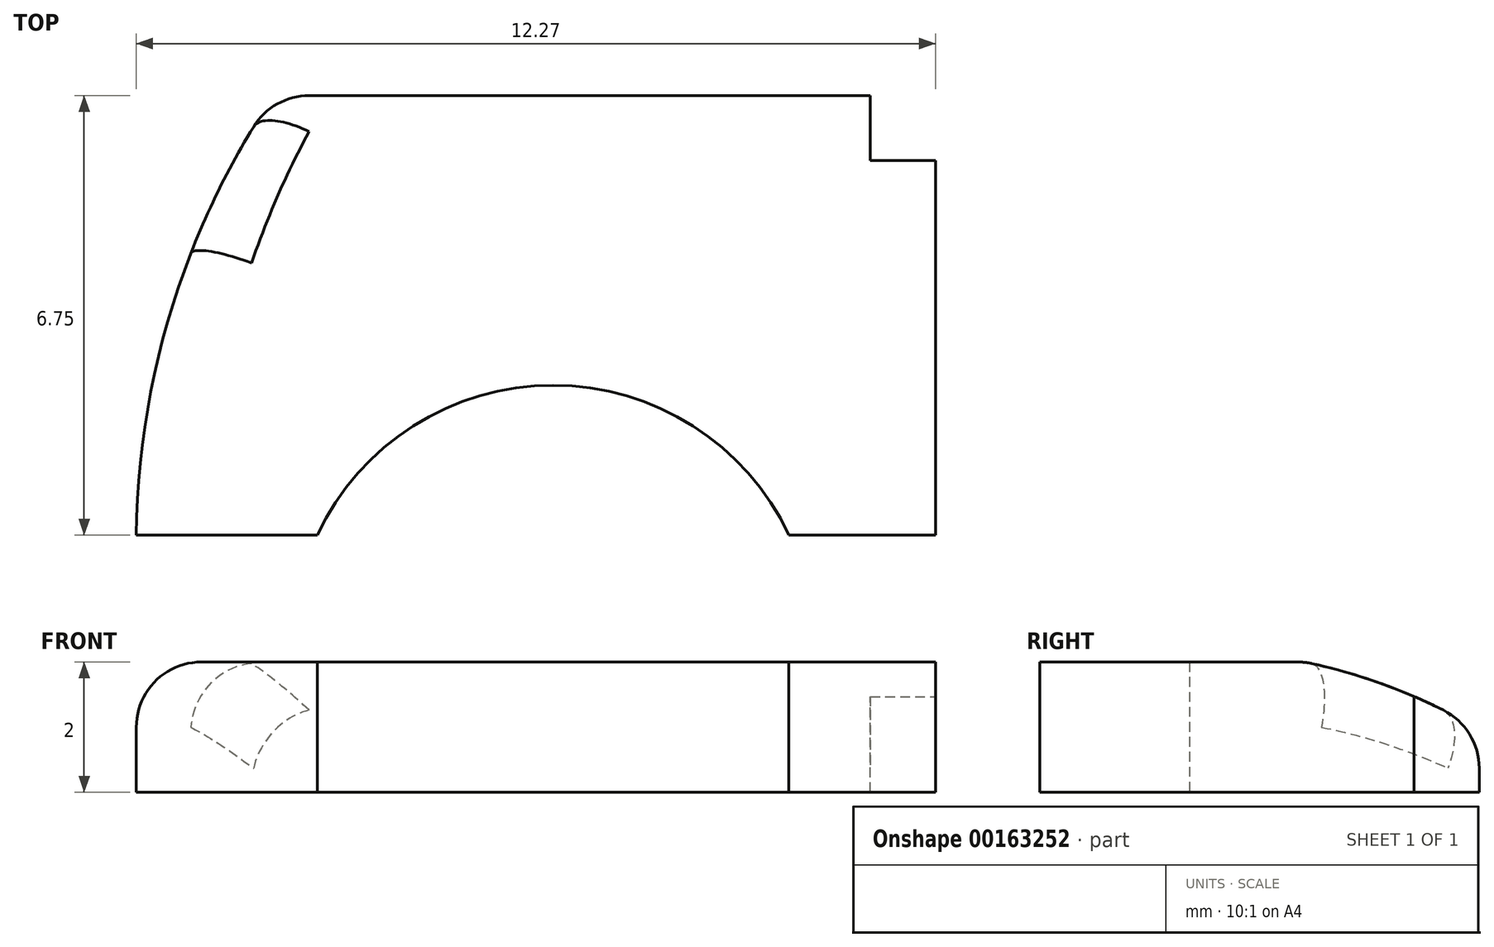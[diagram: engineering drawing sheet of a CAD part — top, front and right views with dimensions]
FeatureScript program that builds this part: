
annotation { "Feature Type Name" : "Feature", "Feature Type Description" : "" }
export const myFeature = defineFeature(function(context is Context, id is Id, definition is map)
    precondition{}
    {
        {
            var Q0;
            Q0=qCreatedBy(makeId("Top.planeOp"),FACE);
            var sketch = newSketch(context, id + "F0", { "sketchPlane" : qUnion([Q0])});
            skArc(sketch, "E0", {"start": v(0, 0) * mm, "mid": v(-3.62, 2.3) * mm, "end": v(-7.24, 0) * mm});
            skLineSegment(sketch, "E1", {"start": v(-7.24, 0) * mm, "end": v(-10.02, 0) * mm});
            skArc(sketch, "E2", {"start": v(-7.91, 6.75) * mm, "mid": v(-9.46, 3.53) * mm, "end": v(-10.02, 0) * mm});
            skLineSegment(sketch, "E3", {"start": v(-7.91, 6.75) * mm, "end": v(2.25, 6.75) * mm});
            skLineSegment(sketch, "E4", {"start": v(2.25, 6.75) * mm, "end": v(2.25, 0) * mm});
            skLineSegment(sketch, "E5", {"start": v(2.25, 0) * mm, "end": v(0, 0) * mm});
            skSolve(sketch);
        }
        {
            var Q0;
            Q0 = qSketchRegion(id + "F0", true);
            extrude(context, id + "F1", {"entities" : qUnion([Q0]), "depth" : 2 * mm});
        }
        {
            var Q0;
            Q0=makeQuery(id+"F1.opExtrude","SWEPT_FACE",FACE,{"disambiguationData":[OSD([sQuery(id+"F0.wireOp",EDGE,"E4")])]});
            var sketch = newSketch(context, id + "F2", { "sketchPlane" : qUnion([Q0])});
            skLineSegment(sketch, "E6", {"start": v(1.3, 1.98) * mm, "end": v(1.3, 1.98) * mm});
            skArc(sketch, "E7", {"start": v(7.25, 0.64) * mm, "mid": v(5.78, 1.46) * mm, "end": v(4.18, 1.98) * mm});
            skPoint(sketch, "E8.visualSharp", {"position": v(8.37, -0.29) * mm});
            skPoint(sketch, "E9.visualSharp", {"position": v(12.01, -0.29) * mm});
            skPoint(sketch, "E10.visualSharp", {"position": v(4.07, 2) * mm});
            skArc(sketch, "E10.filletArc", {"start": v(4.18, 1.98) * mm, "mid": v(4.07, 2) * mm, "end": v(3.96, 2) * mm});
            skLineSegment(sketch, "E11", {"start": v(5.8, 3.91) * mm, "end": v(3.96, 2) * mm});
            skLineSegment(sketch, "E12", {"start": v(5.8, 3.91) * mm, "end": v(8.9, 2.87) * mm});
            skLineSegment(sketch, "E13", {"start": v(8.9, 2.87) * mm, "end": v(7.25, 0.64) * mm});
            skSolve(sketch);
        }
        {
            var Q0;
            Q0 = qSketchRegion(id + "F2", true);
            extrude(context, id + "F3", {"entities" : qUnion([Q0]), "operationType" : NewBodyOperationType.REMOVE, "endBound" : BoundingType.THROUGH_ALL, "oppositeDirection" : true, "depth" : 25 * mm});
        }
        {
            var Q0;
            Q0=makeQuery(id+"F1.opExtrude","SWEPT_EDGE",EDGE,{"disambiguationData":[OSD([sQuery(id+"F0.wireOp",EDGE,"E2"),sQuery(id+"F0.wireOp",EDGE,"E3")])]});
            var Q1;
            Q1=makeQuery(id+"F3.boolean.opBoolean","INTERSECT",EDGE,{"derivedFrom":[makeQuery(id+"F1.opExtrude","SWEPT_FACE",FACE,{"disambiguationData":[OSD([sQuery(id+"F0.wireOp",EDGE,"E2")])]}),makeQuery(id+"F3.opExtrude","SWEPT_FACE",FACE,{"disambiguationData":[OSD([sQuery(id+"F2.wireOp",EDGE,"E7")])]})]});
            fillet(context, id + "F4", {"entities" : qUnion([Q0, Q1]), "radius" : 1 * mm, "tangentPropagation" : true, "allowEdgeOverflow" : false});
        }
        {
            var Q0;
            {var subQ0=sQuery(id+"F0.wireOp",EDGE,"E2");Q0=makeQuery(id+"F4.opFillet","BLEND_EDGE",EDGE,{"blendedFrom":[makeQuery(id+"F1.opExtrude","SWEPT_EDGE",EDGE,{"disambiguationData":[OSD([subQ0,sQuery(id+"F0.wireOp",EDGE,"E3")])]}),makeQuery(id+"F3.boolean.opBoolean","INTERSECT",EDGE,{"derivedFrom":[makeQuery(id+"F1.opExtrude","SWEPT_FACE",FACE,{"disambiguationData":[OSD([subQ0])]}),makeQuery(id+"F3.opExtrude","SWEPT_FACE",FACE,{"disambiguationData":[OSD([sQuery(id+"F2.wireOp",EDGE,"E7")])]})]})],"blendedInto":[]});}
            fillet(context, id + "F5", {"entities" : qUnion([Q0]), "radius" : 1 * mm, "tangentPropagation" : true, "allowEdgeOverflow" : false});
        }
        {
            var Q0;
            Q0=makeQuery(id+"F1.opExtrude","SWEPT_FACE",FACE,{"disambiguationData":[OSD([sQuery(id+"F0.wireOp",EDGE,"E3")])]});
            var sketch = newSketch(context, id + "F6", { "sketchPlane" : qUnion([Q0])});
            skLineSegment(sketch, "E14.bottom", {"start": v(-2.25, 0) * mm, "end": v(-1.25, 0) * mm});
            skLineSegment(sketch, "E14.top", {"start": v(-2.25, 1.98) * mm, "end": v(-1.25, 1.98) * mm});
            skLineSegment(sketch, "E14.left", {"start": v(-2.25, 0) * mm, "end": v(-2.25, 1.98) * mm});
            skLineSegment(sketch, "E14.right", {"start": v(-1.25, 0) * mm, "end": v(-1.25, 1.98) * mm});
            skSolve(sketch);
        }
        {
            var Q0;
            Q0 = qSketchRegion(id + "F6", true);
            extrude(context, id + "F7", {"entities" : qUnion([Q0]), "operationType" : NewBodyOperationType.REMOVE, "oppositeDirection" : true, "depth" : 1 * mm});
        }
    });
